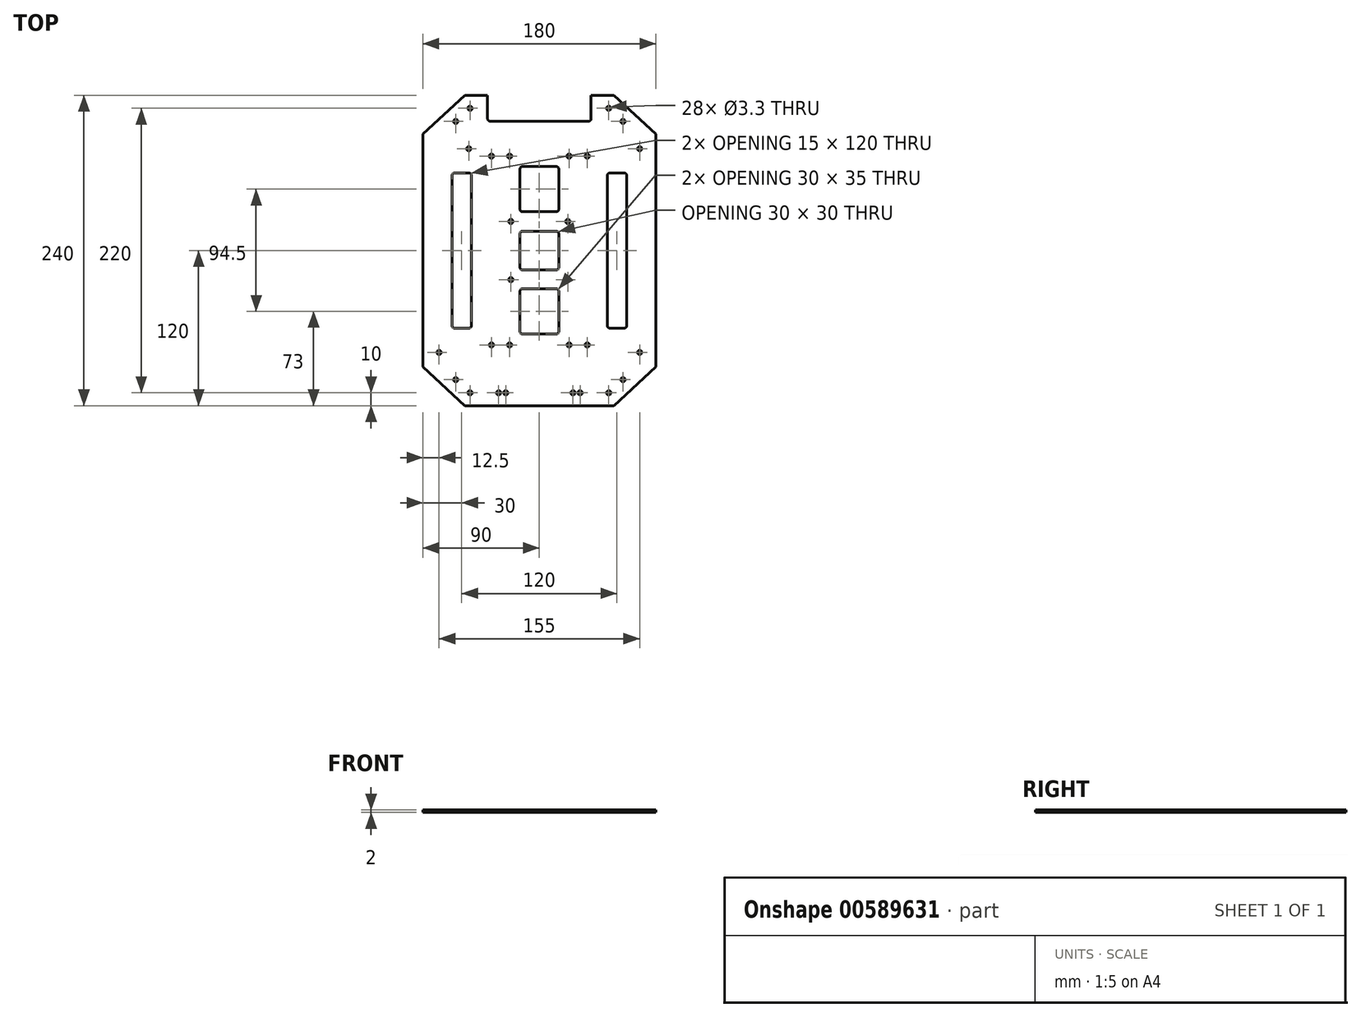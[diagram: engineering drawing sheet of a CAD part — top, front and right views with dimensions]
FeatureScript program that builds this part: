
annotation { "Feature Type Name" : "Feature", "Feature Type Description" : "" }
export const myFeature = defineFeature(function(context is Context, id is Id, definition is map)
    precondition{}
    {
        {
            var Q0;
            Q0=qCreatedBy(makeId("Top.planeOp"),FACE);
            var sketch = newSketch(context, id + "F0", { "sketchPlane" : qUnion([Q0])});
            skPoint(sketch, "E0.middle", {"position": v(0, 0) * mm});
            skLineSegment(sketch, "E1.bottom", {"start": v(23, 73) * mm, "end": v(-23, 73) * mm, "construction": true});
            skLineSegment(sketch, "E1.top", {"start": v(23, -73) * mm, "end": v(-23, -73) * mm, "construction": true});
            skLineSegment(sketch, "E1.left", {"start": v(23, 73) * mm, "end": v(23, -73) * mm, "construction": true});
            skLineSegment(sketch, "E1.right", {"start": v(-23, 73) * mm, "end": v(-23, -73) * mm, "construction": true});
            skPoint(sketch, "E2", {"position": v(-37, -73) * mm});
            skPoint(sketch, "E3", {"position": v(37, -73) * mm});
            skLineSegment(sketch, "E4", {"start": v(0, 0) * mm, "end": v(0, 56.9) * mm, "construction": true});
            skPoint(sketch, "E5", {"position": v(-54.58, 78.75) * mm});
            skPoint(sketch, "E6", {"position": v(37, 73) * mm});
            skLineSegment(sketch, "E7.bottom", {"start": v(90, 90) * mm, "end": v(-90, 90) * mm});
            skLineSegment(sketch, "E7.top", {"start": v(90, -90) * mm, "end": v(-90, -90) * mm});
            skLineSegment(sketch, "E7.left", {"start": v(90, 90) * mm, "end": v(90, -90) * mm});
            skLineSegment(sketch, "E7.right", {"start": v(-90, 90) * mm, "end": v(-90, -90) * mm});
            skPoint(sketch, "E8", {"position": v(-77.5, -78.75) * mm});
            skPoint(sketch, "E9", {"position": v(77.5, -78.75) * mm});
            skPoint(sketch, "E10", {"position": v(77.5, 78.75) * mm});
            skLineSegment(sketch, "E11", {"start": v(-90, 90) * mm, "end": v(-57.5, 120) * mm});
            skLineSegment(sketch, "E12", {"start": v(-57.5, 120) * mm, "end": v(57.5, 120) * mm});
            skLineSegment(sketch, "E13", {"start": v(57.5, 120) * mm, "end": v(90, 90) * mm});
            skLineSegment(sketch, "E14", {"start": v(-90, -90) * mm, "end": v(-57.5, -120) * mm});
            skLineSegment(sketch, "E15", {"start": v(-57.5, -120) * mm, "end": v(57.5, -120) * mm});
            skLineSegment(sketch, "E16", {"start": v(57.5, -120) * mm, "end": v(90, -90) * mm});
            skPoint(sketch, "E17", {"position": v(-37, 73) * mm});
            skSolve(sketch);
        }
        {
            var Q0;
            Q0=makeQuery(id+"F0.imprint","IMPRINT",FACE,{"disambiguationData":[TD([[makeQuery(id+"F0.imprint","IMPRINT",EDGE,{"derivedFrom":sQuery(id+"F0.wireOp",EDGE,"E7.bottom")}),1.0]])]});
            var Q1;
            Q1=makeQuery(id+"F0.imprint","IMPRINT",FACE,{"disambiguationData":[TD([[makeQuery(id+"F0.imprint","IMPRINT",EDGE,{"derivedFrom":sQuery(id+"F0.wireOp",EDGE,"E7.bottom")}),-1.0]])]});
            var Q2;
            Q2=makeQuery(id+"F0.imprint","IMPRINT",FACE,{"disambiguationData":[TD([[makeQuery(id+"F0.imprint","IMPRINT",EDGE,{"derivedFrom":sQuery(id+"F0.wireOp",EDGE,"E7.top")}),1.0]])]});
            extrude(context, id + "F1", {"entities" : qUnion([Q0, Q1, Q2]), "depth" : 2 * mm, "offsetDistance" : 25 * mm});
        }
        {
            var Q0;
            Q0=sQuery(id+"F0.wireOp",VERTEX,"E1.right.start");
            var Q1;
            Q1=sQuery(id+"F0.wireOp",VERTEX,"E1.left.start");
            var Q2;
            Q2=sQuery(id+"F0.wireOp",VERTEX,"E1.left.end");
            var Q3;
            Q3=sQuery(id+"F0.wireOp",VERTEX,"E1.right.end");
            var Q4;
            Q4=sQuery(id+"F0.wireOp",VERTEX,"E5");
            var Q5;
            Q5=sQuery(id+"F0.wireOp",VERTEX,"E6");
            var Q6;
            Q6=sQuery(id+"F0.wireOp",VERTEX,"E10");
            var Q7;
            Q7=sQuery(id+"F0.wireOp",VERTEX,"E8");
            var Q8;
            Q8=sQuery(id+"F0.wireOp",VERTEX,"E2");
            var Q9;
            Q9=sQuery(id+"F0.wireOp",VERTEX,"E9");
            var Q10;
            Q10=sQuery(id+"F0.wireOp",VERTEX,"E3");
            var Q11;
            Q11=sQuery(id+"F0.wireOp",VERTEX,"E17");
            var Q12;
            Q12=makeQuery(id+"F1.opExtrude","SWEPT_BODY",BODY,{"disambiguationData":[OSD([sQuery(id+"F0.wireOp",EDGE,"E7.left"),sQuery(id+"F0.wireOp",EDGE,"E7.right"),sQuery(id+"F0.wireOp",EDGE,"E11"),sQuery(id+"F0.wireOp",EDGE,"E12"),sQuery(id+"F0.wireOp",EDGE,"E13"),sQuery(id+"F0.wireOp",EDGE,"E14"),sQuery(id+"F0.wireOp",EDGE,"E15"),sQuery(id+"F0.wireOp",EDGE,"E16")])]});
            hole(context, id + "F2", {"style" : HoleStyle.SIMPLE, "endStyle" : HoleEndStyle.THROUGH, "oppositeDirection" : true, "standardTappedOrClearance" : lookupTablePath({ "standard" : "ISO", "fit" : "Normal", "size" : "M3", "type" : "Clearance" }), "standardBlindInLast" : lookupTablePath({ "fit" : "Standard", "standard" : "ISO", "size" : "M3", "type" : "Clearance" }), "holeDiameter" : 3.3 * mm, "majorDiameter" : 5 * mm, "isTappedThrough" : true, "tappedDepth" : 6.2 * mm, "tapClearance" : 3, "locations" : qUnion([Q0, Q1, Q2, Q3, Q4, Q5, Q6, Q7, Q8, Q9, Q10, Q11]), "scope" : qUnion([Q12])});
        }
        {
            var Q0;
            Q0=qCreatedBy(makeId("Top.planeOp"),FACE);
            var sketch = newSketch(context, id + "F3", { "sketchPlane" : qUnion([Q0])});
            skPoint(sketch, "E18", {"position": v(-64.61, -99.83) * mm});
            skPoint(sketch, "E19", {"position": v(-53.6, -110) * mm});
            skLineSegment(sketch, "E20", {"start": v(0, 0) * mm, "end": v(0, 68.16) * mm, "construction": true});
            skPoint(sketch, "E21.MirrorP", {"position": v(64.61, -99.83) * mm});
            skPoint(sketch, "E22.MirrorP", {"position": v(53.6, -110) * mm});
            skLineSegment(sketch, "E23", {"start": v(0, 0) * mm, "end": v(123.35, 0) * mm, "construction": true});
            skPoint(sketch, "E24.MirrorP", {"position": v(-64.61, 99.83) * mm});
            skPoint(sketch, "E25.MirrorP", {"position": v(-53.6, 110) * mm});
            skPoint(sketch, "E26.MirrorP", {"position": v(53.6, 110) * mm});
            skPoint(sketch, "E27.MirrorP", {"position": v(64.61, 99.83) * mm});
            skSolve(sketch);
        }
        {
            var Q0;
            Q0=sQuery(id+"F3.wireOp",VERTEX,"E18");
            var Q1;
            Q1=sQuery(id+"F3.wireOp",VERTEX,"E19");
            var Q2;
            Q2=sQuery(id+"F3.wireOp",VERTEX,"E22.MirrorP");
            var Q3;
            Q3=sQuery(id+"F3.wireOp",VERTEX,"E21.MirrorP");
            var Q4;
            Q4=sQuery(id+"F3.wireOp",VERTEX,"E27.MirrorP");
            var Q5;
            Q5=sQuery(id+"F3.wireOp",VERTEX,"E26.MirrorP");
            var Q6;
            Q6=sQuery(id+"F3.wireOp",VERTEX,"E25.MirrorP");
            var Q7;
            Q7=sQuery(id+"F3.wireOp",VERTEX,"E24.MirrorP");
            var Q8;
            Q8=makeQuery(id+"F1.opExtrude","SWEPT_BODY",BODY,{"disambiguationData":[OSD([sQuery(id+"F0.wireOp",EDGE,"E7.left"),sQuery(id+"F0.wireOp",EDGE,"E7.right"),sQuery(id+"F0.wireOp",EDGE,"E11"),sQuery(id+"F0.wireOp",EDGE,"E12"),sQuery(id+"F0.wireOp",EDGE,"E13"),sQuery(id+"F0.wireOp",EDGE,"E14"),sQuery(id+"F0.wireOp",EDGE,"E15"),sQuery(id+"F0.wireOp",EDGE,"E16")])]});
            hole(context, id + "F4", {"style" : HoleStyle.SIMPLE, "endStyle" : HoleEndStyle.THROUGH, "oppositeDirection" : true, "standardTappedOrClearance" : lookupTablePath({ "standard" : "ISO", "fit" : "Normal", "size" : "M3", "type" : "Clearance" }), "standardBlindInLast" : lookupTablePath({ "fit" : "Standard", "standard" : "ISO", "size" : "M3", "type" : "Clearance" }), "holeDiameter" : 3.3 * mm, "majorDiameter" : 5 * mm, "isTappedThrough" : true, "tappedDepth" : 6.2 * mm, "tapClearance" : 3, "locations" : qUnion([Q0, Q1, Q2, Q3, Q4, Q5, Q6, Q7]), "scope" : qUnion([Q8])});
        }
        {
            var Q0;
            Q0=qCreatedBy(makeId("Top.planeOp"),FACE);
            var sketch = newSketch(context, id + "F5", { "sketchPlane" : qUnion([Q0])});
            skLineSegment(sketch, "E28.bottom", {"start": v(22, 22.5) * mm, "end": v(-22, 22.5) * mm, "construction": true});
            skLineSegment(sketch, "E28.top", {"start": v(22, -22.5) * mm, "end": v(-22, -22.5) * mm, "construction": true});
            skLineSegment(sketch, "E28.left", {"start": v(22, 22.5) * mm, "end": v(22, -22.5) * mm, "construction": true});
            skLineSegment(sketch, "E28.right", {"start": v(-22, 22.5) * mm, "end": v(-22, -22.5) * mm, "construction": true});
            skPoint(sketch, "E28.middle", {"position": v(0, 0) * mm});
            skPoint(sketch, "E29", {"position": v(25.98, -110) * mm});
            skPoint(sketch, "E30", {"position": v(31.48, -110) * mm});
            skLineSegment(sketch, "E31", {"start": v(0, 0) * mm, "end": v(0, 53.62) * mm, "construction": true});
            skPoint(sketch, "E32.MirrorP", {"position": v(-31.48, -110) * mm});
            skPoint(sketch, "E33.MirrorP", {"position": v(-25.98, -110) * mm});
            skSolve(sketch);
        }
        {
            var Q0;
            Q0=sQuery(id+"F5.wireOp",VERTEX,"E28.right.start");
            var Q1;
            Q1=sQuery(id+"F5.wireOp",VERTEX,"E28.bottom.start");
            var Q2;
            Q2=sQuery(id+"F5.wireOp",VERTEX,"E28.left.end");
            var Q3;
            Q3=sQuery(id+"F5.wireOp",VERTEX,"E28.right.end");
            var Q4;
            Q4=sQuery(id+"F5.wireOp",VERTEX,"E29");
            var Q5;
            Q5=sQuery(id+"F5.wireOp",VERTEX,"E30");
            var Q6;
            Q6=sQuery(id+"F5.wireOp",VERTEX,"E33.MirrorP");
            var Q7;
            Q7=sQuery(id+"F5.wireOp",VERTEX,"E32.MirrorP");
            var Q8;
            Q8=makeQuery(id+"F1.opExtrude","SWEPT_BODY",BODY,{"disambiguationData":[OSD([sQuery(id+"F0.wireOp",EDGE,"E7.left"),sQuery(id+"F0.wireOp",EDGE,"E7.right"),sQuery(id+"F0.wireOp",EDGE,"E11"),sQuery(id+"F0.wireOp",EDGE,"E12"),sQuery(id+"F0.wireOp",EDGE,"E13"),sQuery(id+"F0.wireOp",EDGE,"E14"),sQuery(id+"F0.wireOp",EDGE,"E15"),sQuery(id+"F0.wireOp",EDGE,"E16")])]});
            hole(context, id + "F6", {"style" : HoleStyle.SIMPLE, "endStyle" : HoleEndStyle.THROUGH, "oppositeDirection" : true, "standardTappedOrClearance" : lookupTablePath({ "standard" : "ISO", "fit" : "Normal", "size" : "M3", "type" : "Clearance" }), "standardBlindInLast" : lookupTablePath({ "fit" : "Standard", "standard" : "ISO", "size" : "M3", "type" : "Clearance" }), "holeDiameter" : 3.3 * mm, "majorDiameter" : 5 * mm, "isTappedThrough" : true, "tappedDepth" : 6.2 * mm, "tapClearance" : 3, "locations" : qUnion([Q0, Q1, Q2, Q3, Q4, Q5, Q6, Q7]), "scope" : qUnion([Q8])});
        }
        {
            var Q0;
            Q0=qCreatedBy(makeId("Top.planeOp"),FACE);
            var sketch = newSketch(context, id + "F7", { "sketchPlane" : qUnion([Q0])});
            skLineSegment(sketch, "E34.bottom", {"start": v(15, 15) * mm, "end": v(-15, 15) * mm});
            skLineSegment(sketch, "E34.top", {"start": v(15, -15) * mm, "end": v(-15, -15) * mm});
            skLineSegment(sketch, "E34.left", {"start": v(15, 15) * mm, "end": v(15, -15) * mm});
            skLineSegment(sketch, "E34.right", {"start": v(-15, 15) * mm, "end": v(-15, -15) * mm});
            skPoint(sketch, "E34.middle", {"position": v(0, 0) * mm});
            skLineSegment(sketch, "E35.bottom", {"start": v(15, 30) * mm, "end": v(-15, 30) * mm});
            skLineSegment(sketch, "E35.top", {"start": v(15, 65) * mm, "end": v(-15, 65) * mm});
            skLineSegment(sketch, "E35.left", {"start": v(15, 30) * mm, "end": v(15, 65) * mm});
            skLineSegment(sketch, "E35.right", {"start": v(-15, 30) * mm, "end": v(-15, 65) * mm});
            skPoint(sketch, "E35.middle", {"position": v(0, 47.5) * mm});
            skLineSegment(sketch, "E36.bottom", {"start": v(15, -29.5) * mm, "end": v(-15, -29.5) * mm});
            skLineSegment(sketch, "E36.top", {"start": v(15, -64.5) * mm, "end": v(-15, -64.5) * mm});
            skLineSegment(sketch, "E36.left", {"start": v(15, -29.5) * mm, "end": v(15, -64.5) * mm});
            skLineSegment(sketch, "E36.right", {"start": v(-15, -29.5) * mm, "end": v(-15, -64.5) * mm});
            skPoint(sketch, "E36.middle", {"position": v(0, -47) * mm});
            skLineSegment(sketch, "E37.bottom", {"start": v(-52.5, 60) * mm, "end": v(-67.5, 60) * mm});
            skLineSegment(sketch, "E37.top", {"start": v(-52.5, -60) * mm, "end": v(-67.5, -60) * mm});
            skLineSegment(sketch, "E37.left", {"start": v(-52.5, 60) * mm, "end": v(-52.5, -60) * mm});
            skLineSegment(sketch, "E37.right", {"start": v(-67.5, 60) * mm, "end": v(-67.5, -60) * mm});
            skPoint(sketch, "E37.middle", {"position": v(-60, 0) * mm});
            skLineSegment(sketch, "E38.bottom", {"start": v(67.5, 60) * mm, "end": v(52.5, 60) * mm});
            skLineSegment(sketch, "E38.top", {"start": v(67.5, -60) * mm, "end": v(52.5, -60) * mm});
            skLineSegment(sketch, "E38.left", {"start": v(67.5, 60) * mm, "end": v(67.5, -60) * mm});
            skLineSegment(sketch, "E38.right", {"start": v(52.5, 60) * mm, "end": v(52.5, -60) * mm});
            skPoint(sketch, "E38.middle", {"position": v(60, 0) * mm});
            skLineSegment(sketch, "E39.bottom", {"start": v(40, 120) * mm, "end": v(-40, 120) * mm});
            skLineSegment(sketch, "E39.top", {"start": v(40, 100) * mm, "end": v(-40, 100) * mm});
            skLineSegment(sketch, "E39.left", {"start": v(40, 120) * mm, "end": v(40, 100) * mm});
            skLineSegment(sketch, "E39.right", {"start": v(-40, 120) * mm, "end": v(-40, 100) * mm});
            skPoint(sketch, "E39.middle", {"position": v(0, 110) * mm});
            skSolve(sketch);
        }
        {
            var Q0;
            Q0 = qSketchRegion(id + "F7", true);
            extrude(context, id + "F8", {"entities" : qUnion([Q0]), "operationType" : NewBodyOperationType.REMOVE, "endBound" : BoundingType.THROUGH_ALL, "depth" : 25 * mm, "offsetDistance" : 25 * mm});
        }
        {
            var Q0;
            Q0=makeQuery(id+"F8.boolean.opBoolean","COPY",EDGE,{"derivedFrom":makeQuery(id+"F8.opExtrude","SWEPT_EDGE",EDGE,{"disambiguationData":[OSD([sQuery(id+"F7.wireOp",EDGE,"E37.top"),sQuery(id+"F7.wireOp",EDGE,"E37.left")])]})});
            var Q1;
            Q1=makeQuery(id+"F8.boolean.opBoolean","COPY",EDGE,{"derivedFrom":makeQuery(id+"F8.opExtrude","SWEPT_EDGE",EDGE,{"disambiguationData":[OSD([sQuery(id+"F7.wireOp",EDGE,"E37.top"),sQuery(id+"F7.wireOp",EDGE,"E37.right")])]})});
            var Q2;
            Q2=makeQuery(id+"F8.boolean.opBoolean","COPY",EDGE,{"derivedFrom":makeQuery(id+"F8.opExtrude","SWEPT_EDGE",EDGE,{"disambiguationData":[OSD([sQuery(id+"F7.wireOp",EDGE,"E37.bottom"),sQuery(id+"F7.wireOp",EDGE,"E37.left")])]})});
            var Q3;
            Q3=makeQuery(id+"F8.boolean.opBoolean","COPY",EDGE,{"derivedFrom":makeQuery(id+"F8.opExtrude","SWEPT_EDGE",EDGE,{"disambiguationData":[OSD([sQuery(id+"F7.wireOp",EDGE,"E35.top"),sQuery(id+"F7.wireOp",EDGE,"E35.left")])]})});
            var Q4;
            Q4=makeQuery(id+"F8.boolean.opBoolean","COPY",EDGE,{"derivedFrom":makeQuery(id+"F8.opExtrude","SWEPT_EDGE",EDGE,{"disambiguationData":[OSD([sQuery(id+"F7.wireOp",EDGE,"E34.bottom"),sQuery(id+"F7.wireOp",EDGE,"E34.left")])]})});
            var Q5;
            Q5=makeQuery(id+"F8.boolean.opBoolean","COPY",EDGE,{"derivedFrom":makeQuery(id+"F8.opExtrude","SWEPT_EDGE",EDGE,{"disambiguationData":[OSD([sQuery(id+"F7.wireOp",EDGE,"E36.bottom"),sQuery(id+"F7.wireOp",EDGE,"E36.left")])]})});
            var Q6;
            Q6=makeQuery(id+"F8.boolean.opBoolean","COPY",EDGE,{"derivedFrom":makeQuery(id+"F8.opExtrude","SWEPT_EDGE",EDGE,{"disambiguationData":[OSD([sQuery(id+"F7.wireOp",EDGE,"E38.bottom"),sQuery(id+"F7.wireOp",EDGE,"E38.left")])]})});
            var Q7;
            Q7=makeQuery(id+"F8.boolean.opBoolean","COPY",EDGE,{"derivedFrom":makeQuery(id+"F8.opExtrude","SWEPT_EDGE",EDGE,{"disambiguationData":[OSD([sQuery(id+"F7.wireOp",EDGE,"E35.bottom"),sQuery(id+"F7.wireOp",EDGE,"E35.left")])]})});
            var Q8;
            Q8=makeQuery(id+"F8.boolean.opBoolean","COPY",EDGE,{"derivedFrom":makeQuery(id+"F8.opExtrude","SWEPT_EDGE",EDGE,{"disambiguationData":[OSD([sQuery(id+"F7.wireOp",EDGE,"E34.top"),sQuery(id+"F7.wireOp",EDGE,"E34.left")])]})});
            var Q9;
            Q9=makeQuery(id+"F8.boolean.opBoolean","COPY",EDGE,{"derivedFrom":makeQuery(id+"F8.opExtrude","SWEPT_EDGE",EDGE,{"disambiguationData":[OSD([sQuery(id+"F7.wireOp",EDGE,"E38.top"),sQuery(id+"F7.wireOp",EDGE,"E38.left")])]})});
            var Q10;
            Q10=makeQuery(id+"F8.boolean.opBoolean","COPY",EDGE,{"derivedFrom":makeQuery(id+"F8.opExtrude","SWEPT_EDGE",EDGE,{"disambiguationData":[OSD([sQuery(id+"F7.wireOp",EDGE,"E39.top"),sQuery(id+"F7.wireOp",EDGE,"E39.left")])]})});
            var Q11;
            Q11=makeQuery(id+"F8.boolean.opBoolean","COPY",EDGE,{"derivedFrom":makeQuery(id+"F8.opExtrude","SWEPT_EDGE",EDGE,{"disambiguationData":[OSD([sQuery(id+"F7.wireOp",EDGE,"E36.top"),sQuery(id+"F7.wireOp",EDGE,"E36.left")])]})});
            var Q12;
            Q12=makeQuery(id+"F8.boolean.opBoolean","COPY",EDGE,{"derivedFrom":makeQuery(id+"F8.opExtrude","SWEPT_EDGE",EDGE,{"disambiguationData":[OSD([sQuery(id+"F7.wireOp",EDGE,"E37.bottom"),sQuery(id+"F7.wireOp",EDGE,"E37.right")])]})});
            var Q13;
            Q13=makeQuery(id+"F8.boolean.opBoolean","COPY",EDGE,{"derivedFrom":makeQuery(id+"F8.opExtrude","SWEPT_EDGE",EDGE,{"disambiguationData":[OSD([sQuery(id+"F7.wireOp",EDGE,"E35.top"),sQuery(id+"F7.wireOp",EDGE,"E35.right")])]})});
            var Q14;
            Q14=makeQuery(id+"F8.boolean.opBoolean","COPY",EDGE,{"derivedFrom":makeQuery(id+"F8.opExtrude","SWEPT_EDGE",EDGE,{"disambiguationData":[OSD([sQuery(id+"F7.wireOp",EDGE,"E34.bottom"),sQuery(id+"F7.wireOp",EDGE,"E34.right")])]})});
            var Q15;
            Q15=makeQuery(id+"F8.boolean.opBoolean","COPY",EDGE,{"derivedFrom":makeQuery(id+"F8.opExtrude","SWEPT_EDGE",EDGE,{"disambiguationData":[OSD([sQuery(id+"F7.wireOp",EDGE,"E36.bottom"),sQuery(id+"F7.wireOp",EDGE,"E36.right")])]})});
            var Q16;
            Q16=makeQuery(id+"F8.boolean.opBoolean","COPY",EDGE,{"derivedFrom":makeQuery(id+"F8.opExtrude","SWEPT_EDGE",EDGE,{"disambiguationData":[OSD([sQuery(id+"F7.wireOp",EDGE,"E38.top"),sQuery(id+"F7.wireOp",EDGE,"E38.right")])]})});
            var Q17;
            Q17=makeQuery(id+"F8.boolean.opBoolean","COPY",EDGE,{"derivedFrom":makeQuery(id+"F8.opExtrude","SWEPT_EDGE",EDGE,{"disambiguationData":[OSD([sQuery(id+"F7.wireOp",EDGE,"E36.top"),sQuery(id+"F7.wireOp",EDGE,"E36.right")])]})});
            var Q18;
            Q18=makeQuery(id+"F8.boolean.opBoolean","COPY",EDGE,{"derivedFrom":makeQuery(id+"F8.opExtrude","SWEPT_EDGE",EDGE,{"disambiguationData":[OSD([sQuery(id+"F7.wireOp",EDGE,"E39.top"),sQuery(id+"F7.wireOp",EDGE,"E39.right")])]})});
            var Q19;
            Q19=makeQuery(id+"F8.boolean.opBoolean","COPY",EDGE,{"derivedFrom":makeQuery(id+"F8.opExtrude","SWEPT_EDGE",EDGE,{"disambiguationData":[OSD([sQuery(id+"F7.wireOp",EDGE,"E34.top"),sQuery(id+"F7.wireOp",EDGE,"E34.right")])]})});
            var Q20;
            Q20=makeQuery(id+"F8.boolean.opBoolean","COPY",EDGE,{"derivedFrom":makeQuery(id+"F8.opExtrude","SWEPT_EDGE",EDGE,{"disambiguationData":[OSD([sQuery(id+"F7.wireOp",EDGE,"E35.bottom"),sQuery(id+"F7.wireOp",EDGE,"E35.right")])]})});
            var Q21;
            Q21=makeQuery(id+"F8.boolean.opBoolean","COPY",EDGE,{"derivedFrom":makeQuery(id+"F8.opExtrude","SWEPT_EDGE",EDGE,{"disambiguationData":[OSD([sQuery(id+"F7.wireOp",EDGE,"E38.bottom"),sQuery(id+"F7.wireOp",EDGE,"E38.right")])]})});
            fillet(context, id + "F9", {"entities" : qUnion([Q0, Q1, Q2, Q3, Q4, Q5, Q6, Q7, Q8, Q9, Q10, Q11, Q12, Q13, Q14, Q15, Q16, Q17, Q18, Q19, Q20, Q21]), "radius" : 2 * mm, "tangentPropagation" : true, "allowEdgeOverflow" : false});
        }
    });
